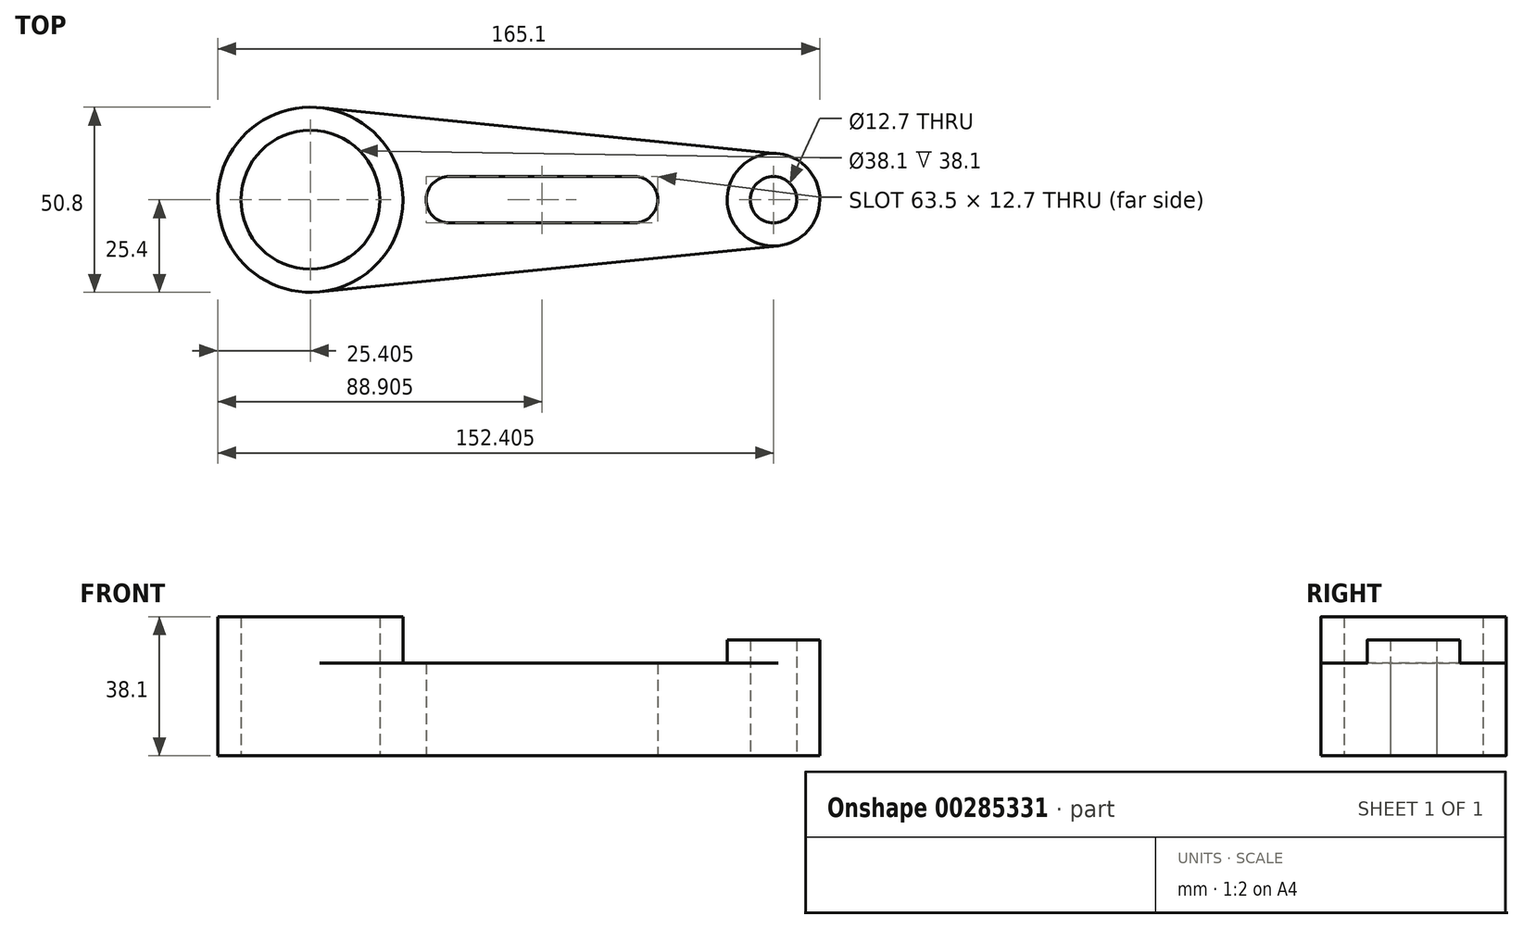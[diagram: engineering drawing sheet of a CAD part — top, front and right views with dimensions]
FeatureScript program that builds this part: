
annotation { "Feature Type Name" : "Feature", "Feature Type Description" : "" }
export const myFeature = defineFeature(function(context is Context, id is Id, definition is map)
    precondition{}
    {
        {
            var Q0;
            Q0=qCreatedBy(makeId("Top.planeOp"),FACE);
            var sketch = newSketch(context, id + "F0", { "sketchPlane" : qUnion([Q0])});
            skCircle(sketch, "E0", {"center": v(-19.8, 0) * mm, "radius": 25.4 * mm});
            skCircle(sketch, "E1", {"center": v(107.2, 0) * mm, "radius": 12.7 * mm});
            skCircle(sketch, "E2", {"center": v(107.2, 0) * mm, "radius": 6.35 * mm});
            skCircle(sketch, "E3", {"center": v(-19.8, 0) * mm, "radius": 19.05 * mm});
            skLineSegment(sketch, "E4", {"start": v(-17.26, 25.27) * mm, "end": v(108.47, 12.64) * mm});
            skLineSegment(sketch, "E5", {"start": v(108.47, -12.64) * mm, "end": v(-17.26, -25.27) * mm});
            skLineSegment(sketch, "E6.bottom", {"start": v(18.3, 6.35) * mm, "end": v(69.1, 6.35) * mm});
            skLineSegment(sketch, "E6.top", {"start": v(18.3, -6.35) * mm, "end": v(69.1, -6.35) * mm});
            skLineSegment(sketch, "E6.left", {"start": v(18.3, 6.35) * mm, "end": v(18.3, -6.35) * mm, "construction": true});
            skLineSegment(sketch, "E6.right", {"start": v(69.1, 6.35) * mm, "end": v(69.1, -6.35) * mm, "construction": true});
            skArc(sketch, "E7", {"start": v(69.1, -6.35) * mm, "mid": v(75.45, 0) * mm, "end": v(69.1, 6.35) * mm});
            skArc(sketch, "E8", {"start": v(18.3, 6.35) * mm, "mid": v(11.95, 0) * mm, "end": v(18.3, -6.35) * mm});
            skSolve(sketch);
        }
        {
            var Q0;
            Q0=makeQuery(id+"F0.imprint","IMPRINT",FACE,{"disambiguationData":[TD([[makeQuery(id+"F0.imprint","IMPRINT",EDGE,{"derivedFrom":sQuery(id+"F0.wireOp",EDGE,"E2")}),-1.0]])]});
            extrude(context, id + "F1", {"entities" : qUnion([Q0]), "depth" : 31.75 * mm});
        }
        {
            var Q0;
            {var subQ1=sQuery(id+"F0.wireOp",EDGE,"E4");Q0=makeQuery(id+"F0.imprint","IMPRINT",FACE,{"disambiguationData":[TD([[makeQuery(id+"F0.imprint","IMPRINT",EDGE,{"derivedFrom":subQ1}),-1.0]])]});}
            extrude(context, id + "F2", {"entities" : qUnion([Q0]), "operationType" : NewBodyOperationType.ADD, "depth" : 25.4 * mm});
        }
        {
            var Q0;
            Q0=makeQuery(id+"F0.imprint","IMPRINT",FACE,{"disambiguationData":[TD([[makeQuery(id+"F0.imprint","IMPRINT",EDGE,{"derivedFrom":sQuery(id+"F0.wireOp",EDGE,"E3")}),-1.0]])]});
            extrude(context, id + "F3", {"entities" : qUnion([Q0]), "operationType" : NewBodyOperationType.ADD, "depth" : 38.1 * mm});
        }
    });
